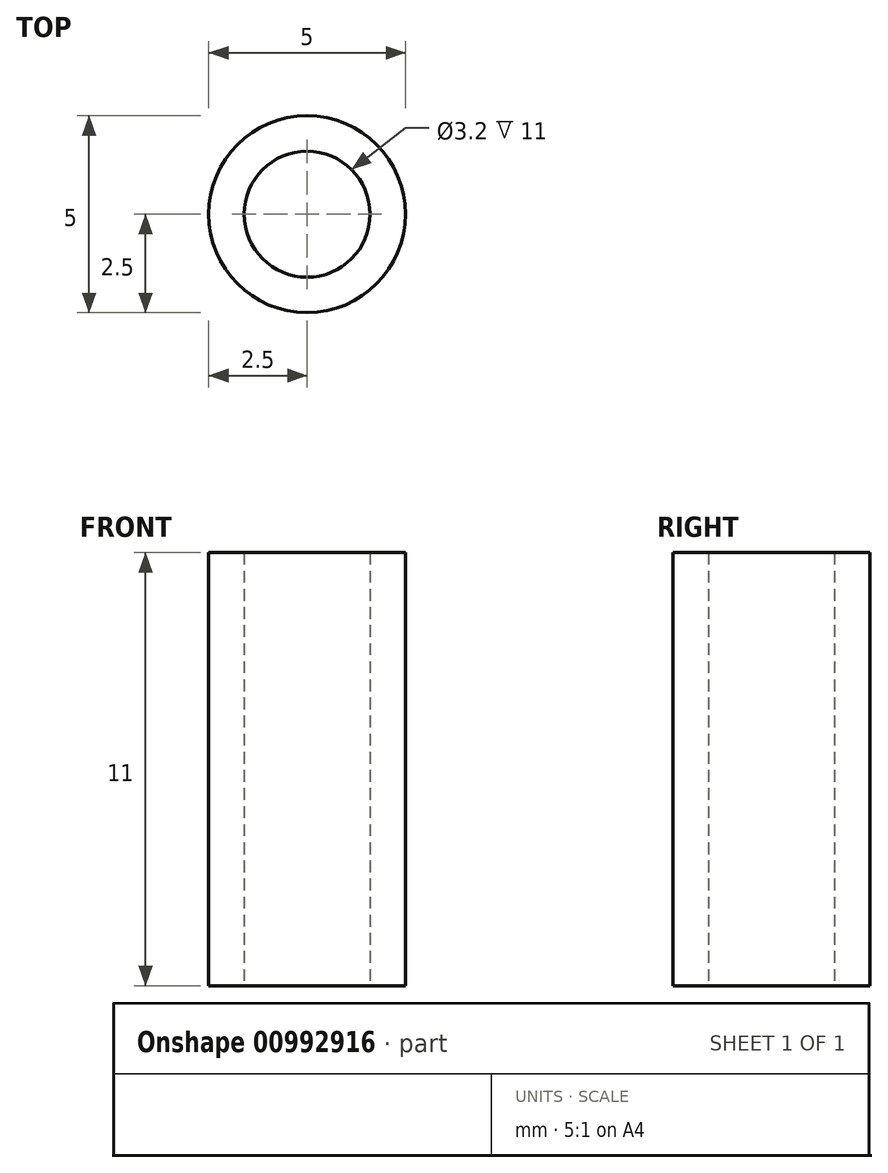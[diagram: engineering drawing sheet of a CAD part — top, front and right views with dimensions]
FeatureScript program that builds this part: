
annotation { "Feature Type Name" : "Feature", "Feature Type Description" : "" }
export const myFeature = defineFeature(function(context is Context, id is Id, definition is map)
    precondition{}
    {
        {
            var Q0;
            Q0=qCreatedBy(makeId("Top.planeOp"),FACE);
            var sketch = newSketch(context, id + "F0", { "sketchPlane" : qUnion([Q0])});
            skCircle(sketch, "E0", {"center": v(0, 0) * mm, "radius": 1.6 * mm});
            skCircle(sketch, "E1", {"center": v(0, 0) * mm, "radius": 2.5 * mm});
            skSolve(sketch);
        }
        {
            var Q0;
            Q0=makeQuery(id+"F0.imprint","IMPRINT",FACE,{"disambiguationData":[TD([[makeQuery(id+"F0.imprint","IMPRINT",EDGE,{"derivedFrom":sQuery(id+"F0.wireOp",EDGE,"E0")}),-1.0]])]});
            extrude(context, id + "F1", {"entities" : qUnion([Q0]), "depth" : 11 * mm, "offsetDistance" : 25 * mm});
        }
    });
